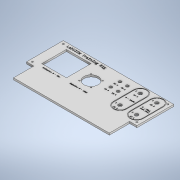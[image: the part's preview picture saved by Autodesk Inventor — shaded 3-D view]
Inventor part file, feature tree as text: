
AUTODESK INVENTOR PART (.ipt)
format: ipt  version: 2022 (Build 260153000, 153)  size: 2,230,784 bytes
history: native  units: in
note: dims shown in document units (in); Inventor stores cm internally (conversion verified against a paired STEP export)
features: sketch x6, extrude x5, other x1
ambient origin geometry x8: Origin, YZ Plane, XZ Plane, XY Plane, X Axis, Y Axis, Z Axis, Center Point
bodies: Solid1 (feature_tree)
feature tree (12):
  extrude  "Extrusion1"  Depth=2.1654in
  extrude  "Extrusion2"  Depth=0.7874in
  extrude  "Extrusion3"  Depth=5.9055in
  extrude  "Extrusion4"  Depth=0.1969in TaperAngle=0.0deg
  extrude  "Extrusion5"  Depth=2.6378in
  other  "Bend Part3"
  sketch  "Sketch1"  dims[d0=3.937in d1=2.1654in]
  sketch  "Sketch2"  dims[d2=11.811in d3=0.7874in]
  sketch  "Sketch3"  dims[d4=0.7874in d5=5.9055in]
  sketch  "Sketch4"  dims[d6=1.9685in d7=0.1969in d8=0.0in]
  sketch  "Sketch5"  dims[d11=2.6378in d12=2.6378in]
  sketch  "Sketch6"  dims[d13=0.6496in d15=0.9843in d16=1.5354in d17=1.5748in d18=1.5748in d19=1.2598in d20=1.2598in d23=0.6299in d24=0.6299in d25=0.1181in d26=0.1181in d27=0.1181in d28=0.1181in d29=0.374in d30=1.7717in d31=2.1654in d32=0.7874in d34=0.315in d36=0.7874in d37=0.9843in d38=0.7874in d39=1.6535in d40=1.378in d41=0.4331in d42=0.1024in d43=0.0512in d44=0.1024in d45=0.0512in d46=0.1024in d47=0.0512in d48=0.1024in d49=0.0512in d50=0.4331in d51=0.0in d52=0.0in d55=0.1772in d58=0.315in d59=0.315in d60=0.315in d62=0.315in d63=0.3937in d64=0.0in d65=0.6496in d66=0.3937in d67=0.3937in d68=0.1969in d69=0.1969in d70=0.3937in d71=0.2362in d72=0.2362in d73=0.3937in d74=1.063in d75=0.4331in d76=0.4331in d77=0.4331in d79=0.4331in d80=0.3937in d81=0.3937in d82=0.9055in d83=0.9055in d84=0.1575in d85=0.3937in d86=0.0in d87=0.1969in d88=90.0deg d89=1.2598in d90=1.2598in d92=0.0787in d93=0.0787in d94=0.0394in d95=0.0in]
